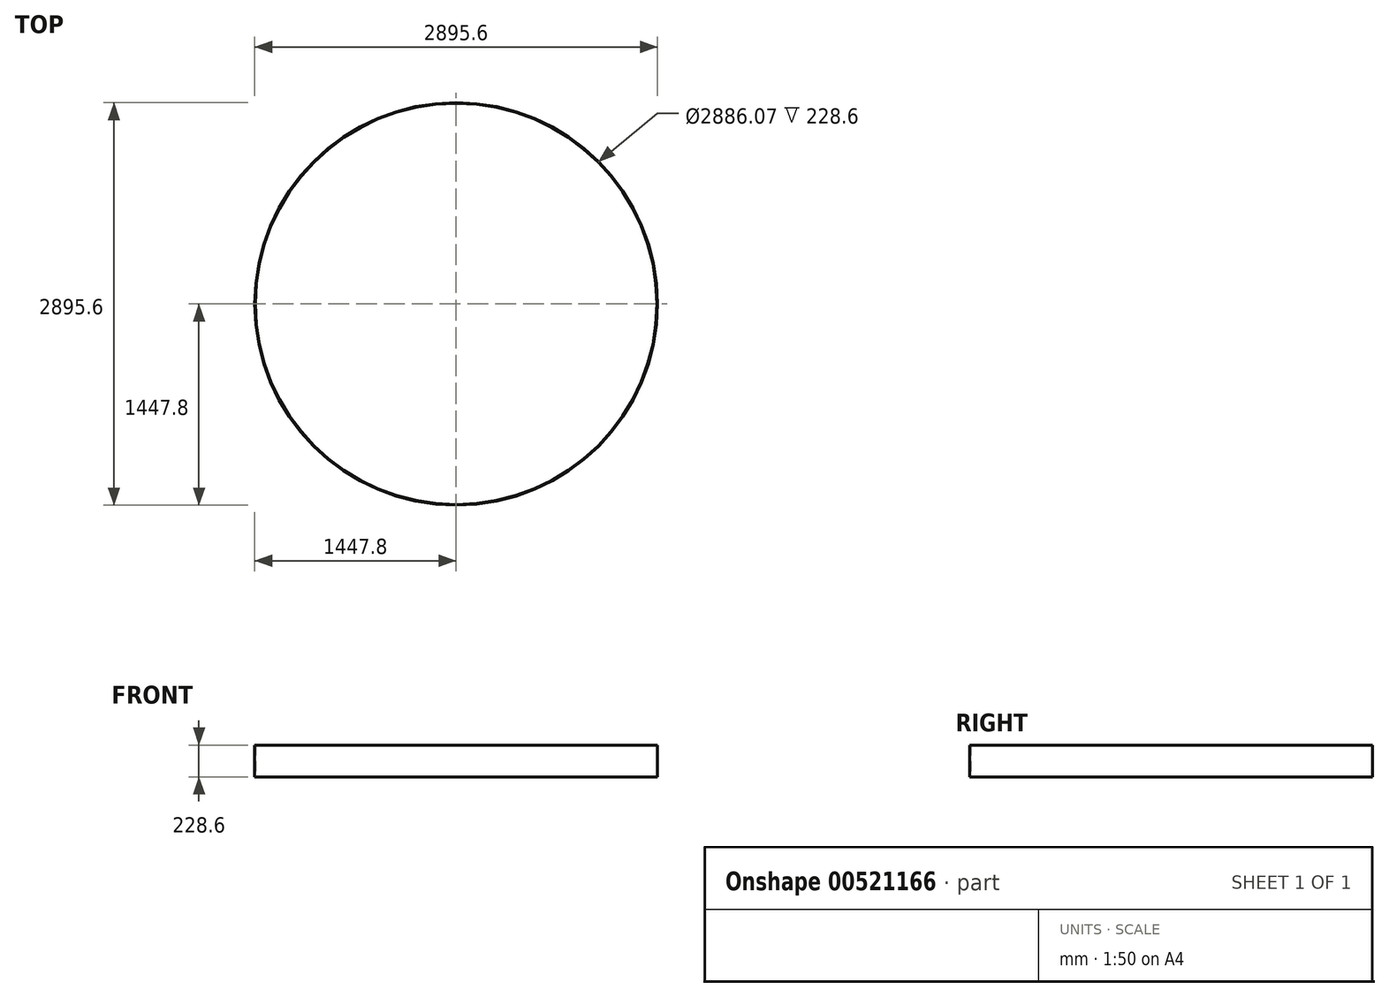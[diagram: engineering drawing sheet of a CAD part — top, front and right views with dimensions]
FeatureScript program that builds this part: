
annotation { "Feature Type Name" : "Feature", "Feature Type Description" : "" }
export const myFeature = defineFeature(function(context is Context, id is Id, definition is map)
    precondition{}
    {
        {
            var Q0;
            Q0=qCreatedBy(makeId("Top.planeOp"),FACE);
            var sketch = newSketch(context, id + "F0", { "sketchPlane" : qUnion([Q0])});
            skCircle(sketch, "E0", {"center": v(0, 0) * mm, "radius": 1447.8 * mm});
            skCircle(sketch, "E1", {"center": v(0, 0) * mm, "radius": 1443.04 * mm});
            skSolve(sketch);
        }
        {
            var Q0;
            Q0=qSketchRegion(id+"F0",true);
            extrude(context, id + "F1", {"entities" : qUnion([Q0]), "depth" : 228.6 * mm});
        }
    });
